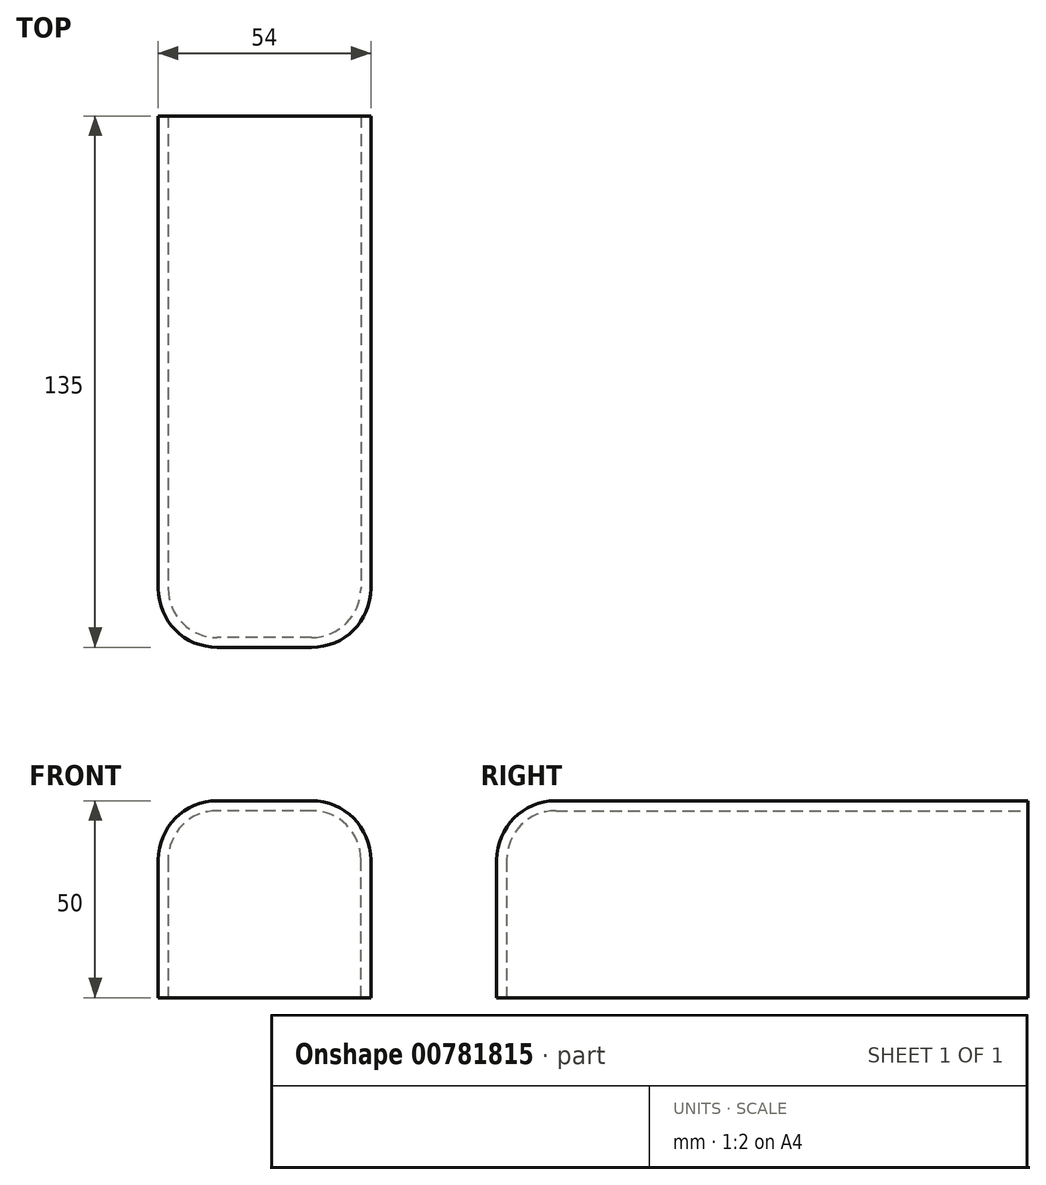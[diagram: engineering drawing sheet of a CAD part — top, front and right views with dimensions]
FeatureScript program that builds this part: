
annotation { "Feature Type Name" : "Feature", "Feature Type Description" : "" }
export const myFeature = defineFeature(function(context is Context, id is Id, definition is map)
    precondition{}
    {
        {
            var Q0;
            Q0=qCreatedBy(makeId("Top.planeOp"),FACE);
            var sketch = newSketch(context, id + "F0", { "sketchPlane" : qUnion([Q0])});
            skLineSegment(sketch, "E0.bottom", {"start": v(27, 75) * mm, "end": v(-27, 75) * mm});
            skLineSegment(sketch, "E0.top", {"start": v(27, -75) * mm, "end": v(-27, -75) * mm});
            skLineSegment(sketch, "E0.left", {"start": v(27, 75) * mm, "end": v(27, -75) * mm});
            skLineSegment(sketch, "E0.right", {"start": v(-27, 75) * mm, "end": v(-27, -75) * mm});
            skPoint(sketch, "E0.middle", {"position": v(0, 0) * mm});
            skSolve(sketch);
        }
        {
            var Q0;
            Q0=qSketchRegion(id+"F0",true);
            extrude(context, id + "F1", {"entities" : qUnion([Q0]), "depth" : 50 * mm, "offsetDistance" : 25 * mm});
        }
        {
            var Q0;
            Q0=makeQuery(id+"F1.opExtrude","SWEPT_EDGE",EDGE,{"disambiguationData":[OSD([sQuery(id+"F0.wireOp",EDGE,"E0.top"),sQuery(id+"F0.wireOp",EDGE,"E0.left")])]});
            var Q1;
            Q1=makeQuery(id+"F1.opExtrude","SWEPT_EDGE",EDGE,{"disambiguationData":[OSD([sQuery(id+"F0.wireOp",EDGE,"E0.top"),sQuery(id+"F0.wireOp",EDGE,"E0.right")])]});
            var Q2;
            Q2=makeQuery(id+"F1.opExtrude","SWEPT_EDGE",EDGE,{"disambiguationData":[OSD([sQuery(id+"F0.wireOp",EDGE,"E0.bottom"),sQuery(id+"F0.wireOp",EDGE,"E0.left")])]});
            var Q3;
            Q3=makeQuery(id+"F1.opExtrude","SWEPT_EDGE",EDGE,{"disambiguationData":[OSD([sQuery(id+"F0.wireOp",EDGE,"E0.bottom"),sQuery(id+"F0.wireOp",EDGE,"E0.right")])]});
            fillet(context, id + "F2", {"entities" : qUnion([Q0, Q1, Q2, Q3]), "radius" : 15 * mm, "tangentPropagation" : true, "allowEdgeOverflow" : false});
        }
        {
            var Q0;
            Q0=makeQuery(id+"F1.opExtrude","CAP_EDGE",EDGE,{"disambiguationData":[OSD([sQuery(id+"F0.wireOp",EDGE,"E0.right")])],"isStart":false});
            fillet(context, id + "F3", {"entities" : qUnion([Q0]), "radius" : 15 * mm, "tangentPropagation" : true, "allowEdgeOverflow" : false});
        }
        {
            var Q0;
            Q0=makeQuery(id+"F1.opExtrude","CAP_FACE",FACE,{"disambiguationData":[OSD([sQuery(id+"F0.wireOp",EDGE,"E0.bottom"),sQuery(id+"F0.wireOp",EDGE,"E0.top"),sQuery(id+"F0.wireOp",EDGE,"E0.left"),sQuery(id+"F0.wireOp",EDGE,"E0.right")])],"isStart":true});
            var sketch = newSketch(context, id + "F4", { "sketchPlane" : qUnion([Q0])});
            skSolve(sketch);
        }
        {
            var Q0;
            {var subQ3=sQuery(id+"F0.wireOp",EDGE,"E0.bottom");Q0=makeQuery(id+"F4.imprint","IMPRINT",FACE,{"disambiguationData":[TD([[makeQuery(id+"F4.imprint","IMPRINT",EDGE,{"derivedFrom":makeQuery(id+"F1.opExtrude","CAP_EDGE",EDGE,{"disambiguationData":[OSD([subQ3])],"isStart":true})}),-1.0]])]});}
            extrude(context, id + "F5", {"entities" : qUnion([Q0]), "operationType" : NewBodyOperationType.ADD, "depth" : 5 * mm, "offsetDistance" : 25 * mm});
        }
        {
            var Q0;
            Q0=qCreatedBy(makeId("Top.planeOp"),FACE);
            var sketch = newSketch(context, id + "F6", { "sketchPlane" : qUnion([Q0])});
            skLineSegment(sketch, "E1.bottom", {"start": v(-62, -99.27) * mm, "end": v(59.1, -99.27) * mm});
            skLineSegment(sketch, "E1.top", {"start": v(-62, 121.66) * mm, "end": v(59.1, 121.66) * mm});
            skLineSegment(sketch, "E1.left", {"start": v(-62, -99.27) * mm, "end": v(-62, 121.66) * mm});
            skLineSegment(sketch, "E1.right", {"start": v(59.1, -99.27) * mm, "end": v(59.1, 121.66) * mm});
            skSolve(sketch);
        }
        {
            var Q0;
            Q0 = qSketchRegion(id + "F6", true);
            extrude(context, id + "F7", {"entities" : qUnion([Q0]), "operationType" : NewBodyOperationType.REMOVE, "endBound" : BoundingType.THROUGH_ALL, "oppositeDirection" : true, "depth" : 25 * mm, "offsetDistance" : 25 * mm});
        }
        {
            var Q0;
            Q0=makeQuery(id+"F7.boolean.opBoolean","COPY",FACE,{"derivedFrom":makeQuery(id+"F7.opExtrude","CAP_FACE",FACE,{"disambiguationData":[OSD([sQuery(id+"F6.wireOp",EDGE,"E1.bottom"),sQuery(id+"F6.wireOp",EDGE,"E1.top"),sQuery(id+"F6.wireOp",EDGE,"E1.left"),sQuery(id+"F6.wireOp",EDGE,"E1.right")])],"isStart":true})});
            var sketch = newSketch(context, id + "F8", { "sketchPlane" : qUnion([Q0])});
            skLineSegment(sketch, "E2.bottom", {"start": v(-62.63, -60) * mm, "end": v(78.77, -60) * mm});
            skLineSegment(sketch, "E2.top", {"start": v(-62.63, -149.87) * mm, "end": v(78.77, -149.87) * mm});
            skLineSegment(sketch, "E2.left", {"start": v(-62.63, -60) * mm, "end": v(-62.63, -149.87) * mm});
            skLineSegment(sketch, "E2.right", {"start": v(78.77, -60) * mm, "end": v(78.77, -149.87) * mm});
            skSolve(sketch);
        }
        {
            var Q0;
            Q0 = qSketchRegion(id + "F8", true);
            extrude(context, id + "F9", {"entities" : qUnion([Q0]), "operationType" : NewBodyOperationType.REMOVE, "endBound" : BoundingType.THROUGH_ALL, "oppositeDirection" : true, "depth" : 25 * mm, "offsetDistance" : 25 * mm});
        }
        {
            var Q0;
            Q0=makeQuery(id+"F7.boolean.opBoolean","COPY",FACE,{"derivedFrom":makeQuery(id+"F7.opExtrude","CAP_FACE",FACE,{"disambiguationData":[OSD([sQuery(id+"F6.wireOp",EDGE,"E1.bottom"),sQuery(id+"F6.wireOp",EDGE,"E1.top"),sQuery(id+"F6.wireOp",EDGE,"E1.left"),sQuery(id+"F6.wireOp",EDGE,"E1.right")])],"isStart":true})});
            var Q1;
            Q1=makeQuery(id+"F9.boolean.opBoolean","COPY",FACE,{"derivedFrom":makeQuery(id+"F9.opExtrude","SWEPT_FACE",FACE,{"disambiguationData":[OSD([sQuery(id+"F8.wireOp",EDGE,"E2.bottom")])]})});
            shell(context, id + "F10", {"entities" : qUnion([Q0, Q1]), "thickness" : 2.5 * mm});
        }
    });
